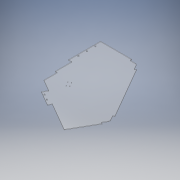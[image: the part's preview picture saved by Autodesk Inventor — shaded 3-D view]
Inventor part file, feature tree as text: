
AUTODESK INVENTOR PART (.ipt)
format: ipt  version: 2019.4 (Build 234330000, 330)  size: 237,056 bytes
history: native  units: mm
features: sketch x7, extrude x6, fillet x1
ambient origin geometry x8: Origin, YZ Plane, XZ Plane, XY Plane, X Axis, Y Axis, Z Axis, Center Point
bodies: Solid1 (feature_tree)
feature tree (14):
  extrude  "Extrusion1"  Depth=303.0mm
  extrude  "Extrusion2"  Depth=16.0mm
  extrude  "Extrusion3"  Depth=30.0mm TaperAngle=360.0deg
  extrude  "Extrusion4"  Depth=151.5mm
  extrude  "Extrusion5"  Depth=152.5mm
  sketch  "Sketch6"  dims[d14=17.0mm d15=3.0mm d16=0.0mm d17=35.0mm]
  extrude  "Extrusion6"  Depth=3.0mm TaperAngle=0.0deg
  fillet  "Fillet1"  Radius=35.0mm
  sketch  "Sketch1"  dims[d0=303.0mm d1=303.0mm]
  sketch  "Sketch2"  dims[d2=8.0mm d3=16.0mm]
  sketch  "Sketch3"  dims[d4=5.0mm d5=30.0mm d7=360.0deg]
  sketch  "Sketch4"  dims[d9=3.0mm d10=0.0mm d11=151.5mm]
  sketch  "Sketch5"  dims[d12=16.0mm d13=152.5mm]
  sketch  "Sketch7"  dims[d18=8.0mm d19=35.0mm d20=8.0mm d21=35.0mm d22=8.0mm d23=35.0mm d24=120.0deg d25=8.0mm d26=3.0mm d27=0.0mm d28=145.0mm d29=30.0deg d30=35.0mm d31=145.0mm d32=90.0deg d33=35.0mm d34=3.0mm d35=0.0mm d36=40.0mm d37=5.5mm d38=30.0mm d40=40.0mm d41=10.0mm d43=10.0mm d45=1.0mm d46=6.0mm d47=30.0mm d48=30.0mm d49=5.5mm d50=5.5mm d51=3.0mm d52=0.0mm d53=7.0mm d54=352.0mm d55=450.0mm d56=100.0mm d57=30.0deg d58=10.5mm d59=90.0deg d60=2.2mm d61=3.0mm d62=30.0deg d63=20.0mm d65=21.0mm d66=20.0mm d68=12.5mm d71=5.0mm d72=0.0mm d73=10.0mm]
